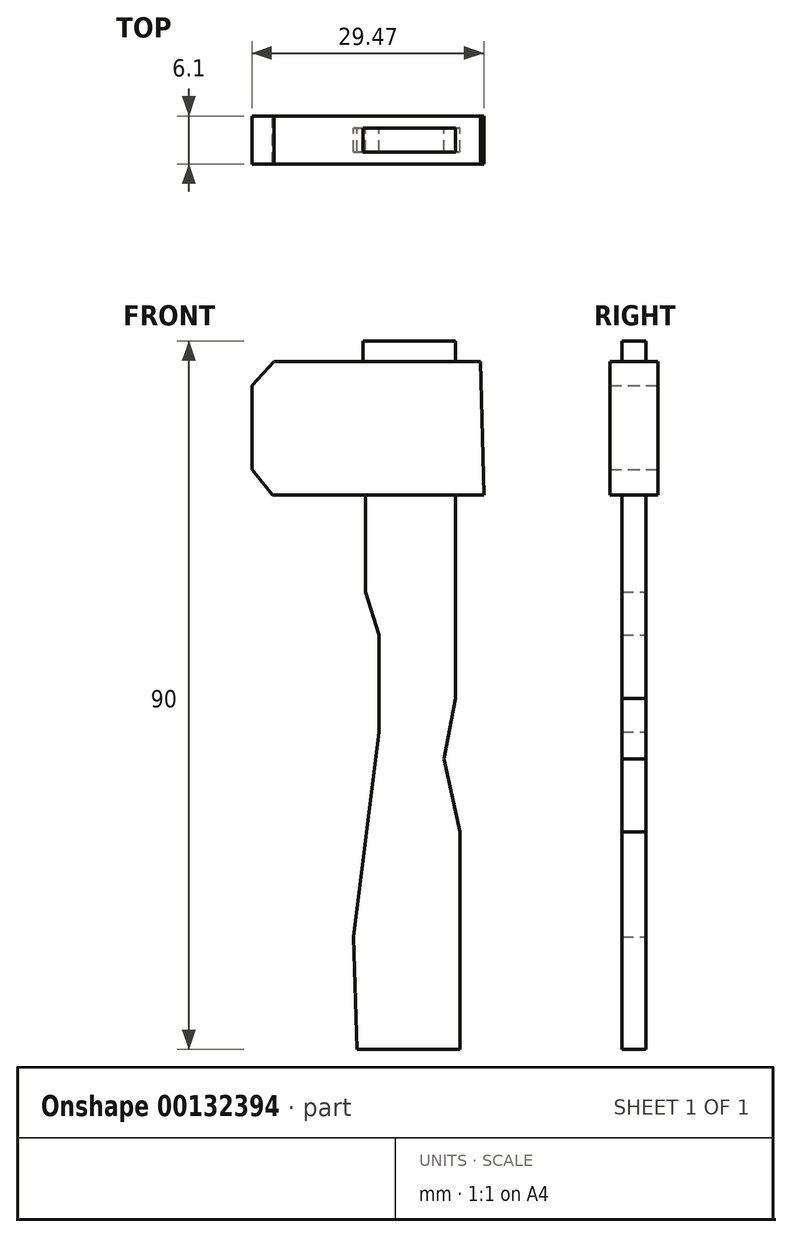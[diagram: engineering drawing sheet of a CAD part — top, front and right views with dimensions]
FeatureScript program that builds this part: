
annotation { "Feature Type Name" : "Feature", "Feature Type Description" : "" }
export const myFeature = defineFeature(function(context is Context, id is Id, definition is map)
    precondition{}
    {
        {
            var Q0;
            Q0=qCreatedBy(makeId("Front.planeOp"),FACE);
            var sketch = newSketch(context, id + "F0", { "sketchPlane" : qUnion([Q0])});
            skLineSegment(sketch, "E0", {"start": v(-6.46, -17.66) * mm, "end": v(6.66, -17.66) * mm});
            skLineSegment(sketch, "E1", {"start": v(6.66, -17.66) * mm, "end": v(6.66, 9.99) * mm});
            skLineSegment(sketch, "E2", {"start": v(6.66, 9.99) * mm, "end": v(4.64, 19.27) * mm});
            skLineSegment(sketch, "E3", {"start": v(4.64, 19.27) * mm, "end": v(6.05, 26.94) * mm});
            skLineSegment(sketch, "E4", {"start": v(6.05, 26.94) * mm, "end": v(6.05, 45.1) * mm});
            skLineSegment(sketch, "E5", {"start": v(9.28, 69.72) * mm, "end": v(-16.95, 69.72) * mm});
            skLineSegment(sketch, "E6", {"start": v(-16.95, 69.72) * mm, "end": v(-19.78, 66.7) * mm});
            skLineSegment(sketch, "E7", {"start": v(-5.35, 40.46) * mm, "end": v(-3.63, 35.01) * mm});
            skLineSegment(sketch, "E8", {"start": v(-3.63, 35.01) * mm, "end": v(-3.63, 22.7) * mm});
            skLineSegment(sketch, "E9", {"start": v(-3.63, 22.7) * mm, "end": v(-6.86, -3.33) * mm});
            skLineSegment(sketch, "E10", {"start": v(-6.86, -3.33) * mm, "end": v(-6.46, -17.66) * mm});
            skLineSegment(sketch, "E11", {"start": v(-5.65, 69.72) * mm, "end": v(-5.65, 72.34) * mm});
            skLineSegment(sketch, "E12", {"start": v(-5.65, 72.34) * mm, "end": v(6.05, 72.34) * mm});
            skLineSegment(sketch, "E13", {"start": v(6.05, 72.34) * mm, "end": v(6.05, 69.72) * mm});
            skLineSegment(sketch, "E14", {"start": v(-19.78, 66.7) * mm, "end": v(-19.78, 56) * mm});
            skLineSegment(sketch, "E15", {"start": v(-19.78, 56) * mm, "end": v(-17.15, 52.77) * mm});
            skLineSegment(sketch, "E16", {"start": v(-17.15, 52.77) * mm, "end": v(9.69, 52.77) * mm});
            skLineSegment(sketch, "E17", {"start": v(6.05, 45.1) * mm, "end": v(6.05, 52.77) * mm});
            skLineSegment(sketch, "E18", {"start": v(6.05, 52.77) * mm, "end": v(9.69, 52.77) * mm});
            skLineSegment(sketch, "E19", {"start": v(9.69, 52.77) * mm, "end": v(9.28, 69.72) * mm});
            skLineSegment(sketch, "E20", {"start": v(-5.35, 40.46) * mm, "end": v(-5.35, 52.77) * mm});
            skSolve(sketch);
        }
        {
            var Q0;
            Q0=makeQuery(id+"F0.imprint","IMPRINT",FACE,{"disambiguationData":[TD([[makeQuery(id+"F0.imprint","IMPRINT",EDGE,{"derivedFrom":sQuery(id+"F0.wireOp",EDGE,"E0")}),1.0]])]});
            var Q1;
            {var subQ0=sQuery(id+"F0.wireOp",EDGE,"E11");Q1=makeQuery(id+"F0.imprint","IMPRINT",FACE,{"disambiguationData":[TD([[makeQuery(id+"F0.imprint","IMPRINT",EDGE,{"derivedFrom":subQ0}),-1.0]])]});}
            extrude(context, id + "F1", {"entities" : qUnion([Q0, Q1]), "endBound" : BoundingType.SYMMETRIC, "depth" : 3.05 * mm});
        }
        {
            var Q0;
            {var subQ0=sQuery(id+"F0.wireOp",EDGE,"E6");Q0=makeQuery(id+"F0.imprint","IMPRINT",FACE,{"disambiguationData":[TD([[makeQuery(id+"F0.imprint","IMPRINT",EDGE,{"derivedFrom":subQ0}),1.0]])]});}
            extrude(context, id + "F2", {"entities" : qUnion([Q0]), "endBound" : BoundingType.SYMMETRIC, "depth" : 6.1 * mm});
        }
    });
